# Revit family: EZS8L
name_source: partatom
category: Plumbing Fixtures
units: mm (PartAtom-declared; Revit-internal decimal feet)

## family parameters
Always vertical = Yes
Cut with Voids When Loaded = No
Part Type = Normal
Room Calculation Point = No
Round Connector Dimension = Use Diameter
Shared = No
Work Plane-Based = No

## types (2) — shared parameters
Activation by = Electronic Front Bubbler Pushbar
Approx. Shipping Weight = 51 lbs
Bubbler Style = Flexi-Guard ® Safety Bubbler
Chilling Capacity = 8.0 GPH
Dimensions (L x W x H) = 18 3/8 inch x 19 inch x 19-13/16 inch
Filter options = Filtered (as standard) (CIVIQ™ staff will recommend a suitable filter based on installation location)
Finish = Light Gray Granite
Full Load Amps = 5
Installation Location = Indoor
Manufacturer = Elkay
Mounting Type = Wall Mount (On Wall)
No. of Stations Served = 1
Power = 115V/60Hz
Rated Watts = 370
Version = 1.0.0.0

## per-type parameters (varying)
| type | Special Features |
| EZS8L | - |
| EZS8LF | Glass Filler Prepped |

note: column(s) folded — value = type name in every type: Model

## geometry (parser evidence)
native form markers: Sweep x11
no freeform markers — native parametric forms only
